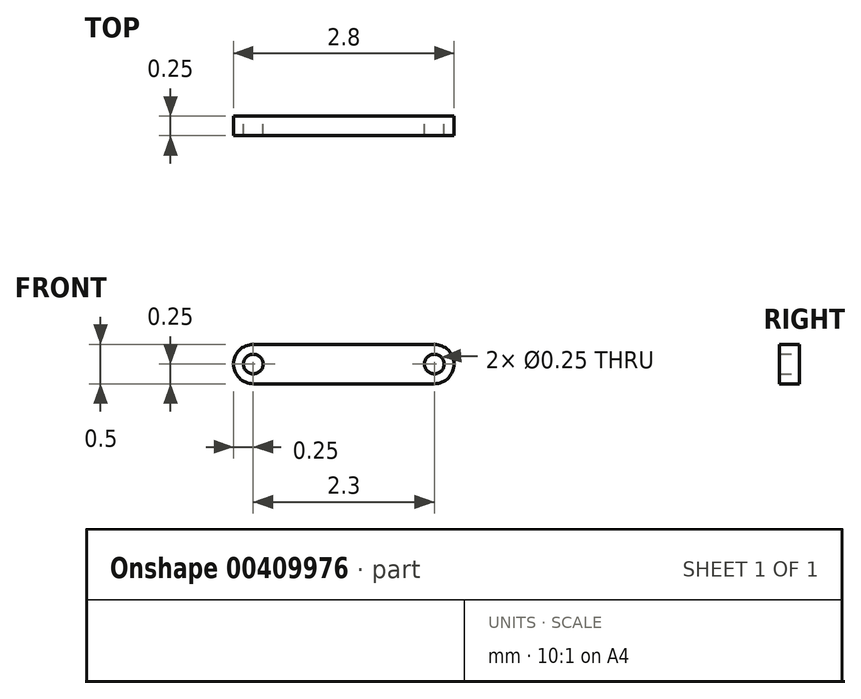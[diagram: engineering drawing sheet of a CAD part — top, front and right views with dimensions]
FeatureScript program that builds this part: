
annotation { "Feature Type Name" : "Feature", "Feature Type Description" : "" }
export const myFeature = defineFeature(function(context is Context, id is Id, definition is map)
    precondition{}
    {
        {
            var Q0;
            Q0=qCreatedBy(makeId("Front.planeOp"),FACE);
            var sketch = newSketch(context, id + "F0", { "sketchPlane" : qUnion([Q0])});
            skArc(sketch, "E0", {"start": v(0, 0.25) * mm, "mid": v(-0.25, 0) * mm, "end": v(0, -0.25) * mm});
            skArc(sketch, "E1", {"start": v(2.3, -0.25) * mm, "mid": v(2.55, 0) * mm, "end": v(2.3, 0.25) * mm});
            skCircle(sketch, "E2", {"center": v(0, 0) * mm, "radius": 0.12 * mm});
            skCircle(sketch, "E3", {"center": v(2.3, 0) * mm, "radius": 0.12 * mm});
            skLineSegment(sketch, "E4", {"start": v(0, 0.25) * mm, "end": v(2.3, 0.25) * mm});
            skLineSegment(sketch, "E5", {"start": v(0, -0.25) * mm, "end": v(2.3, -0.25) * mm});
            skSolve(sketch);
        }
        {
            var Q0;
            Q0=makeQuery(id+"F0.imprint","IMPRINT",FACE,{"disambiguationData":[TD([[makeQuery(id+"F0.imprint","IMPRINT",EDGE,{"derivedFrom":sQuery(id+"F0.wireOp",EDGE,"E0")}),1.0]])]});
            extrude(context, id + "F1", {"entities" : qUnion([Q0]), "depth" : 0.25 * mm});
        }
    });
